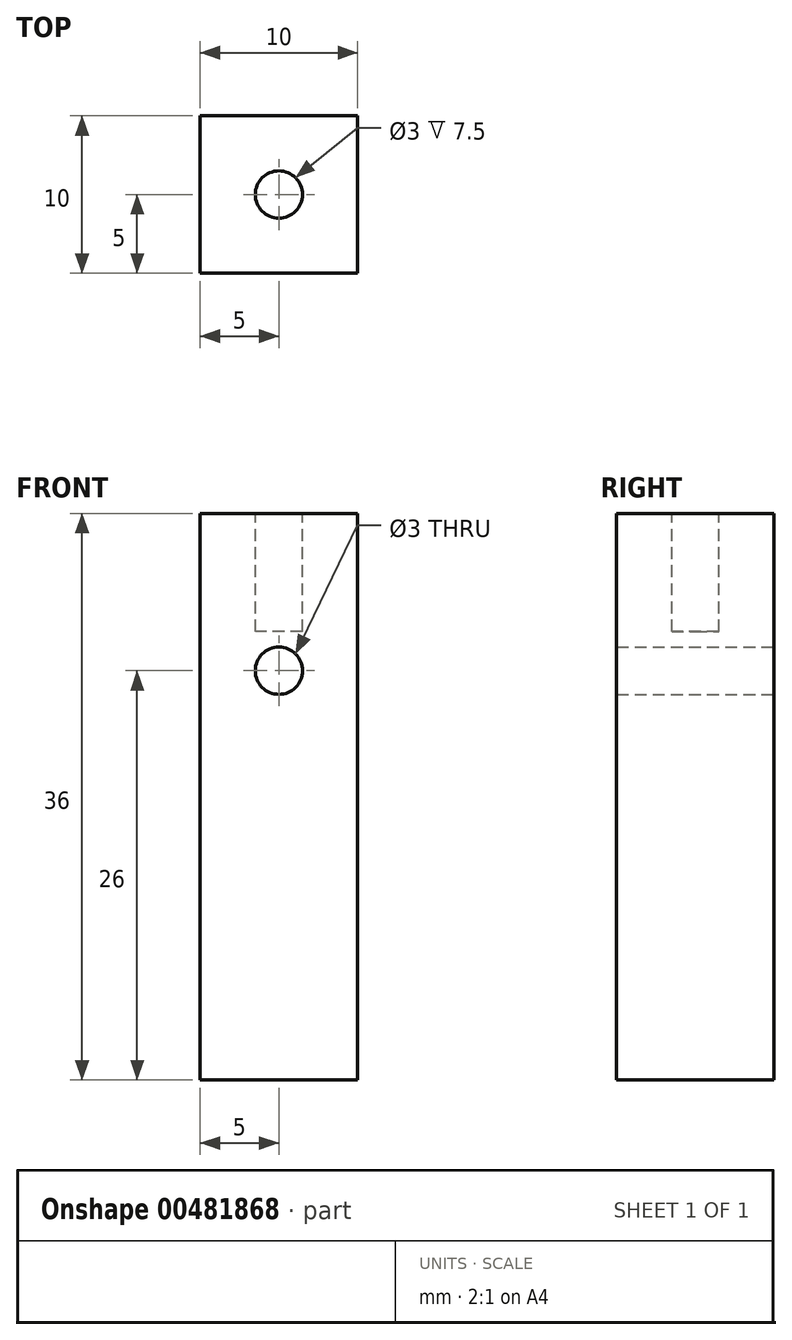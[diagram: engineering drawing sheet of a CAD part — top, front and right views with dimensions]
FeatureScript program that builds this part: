
annotation { "Feature Type Name" : "Feature", "Feature Type Description" : "" }
export const myFeature = defineFeature(function(context is Context, id is Id, definition is map)
    precondition{}
    {
        {
            var Q0;
            Q0=qCreatedBy(makeId("Top.planeOp"),FACE);
            var sketch = newSketch(context, id + "F0", { "sketchPlane" : qUnion([Q0])});
            skLineSegment(sketch, "E0.bottom", {"start": v(-5, -5) * mm, "end": v(5, -5) * mm});
            skLineSegment(sketch, "E0.top", {"start": v(-5, 5) * mm, "end": v(5, 5) * mm});
            skLineSegment(sketch, "E0.left", {"start": v(-5, -5) * mm, "end": v(-5, 5) * mm});
            skLineSegment(sketch, "E0.right", {"start": v(5, -5) * mm, "end": v(5, 5) * mm});
            skPoint(sketch, "E0.middle", {"position": v(0, 0) * mm});
            skSolve(sketch);
        }
        {
            var Q0;
            Q0 = qSketchRegion(id + "F0", true);
            extrude(context, id + "F1", {"entities" : qUnion([Q0]), "endBound" : BoundingType.SYMMETRIC, "depth" : 36 * mm});
        }
        {
            var Q0;
            Q0=makeQuery(id+"F1.opExtrude","CAP_FACE",FACE,{"disambiguationData":[OSD([sQuery(id+"F0.wireOp",EDGE,"E0.bottom"),sQuery(id+"F0.wireOp",EDGE,"E0.top"),sQuery(id+"F0.wireOp",EDGE,"E0.left"),sQuery(id+"F0.wireOp",EDGE,"E0.right")])],"isStart":false});
            var sketch = newSketch(context, id + "F2", { "sketchPlane" : qUnion([Q0])});
            skCircle(sketch, "E1", {"center": v(0, 0) * mm, "radius": 1.5 * mm});
            skSolve(sketch);
        }
        {
            var Q0;
            Q0 = qSketchRegion(id + "F2", true);
            extrude(context, id + "F3", {"entities" : qUnion([Q0]), "operationType" : NewBodyOperationType.REMOVE, "oppositeDirection" : true, "depth" : 7.5 * mm});
        }
        {
            var Q0;
            Q0=qCreatedBy(makeId("Front.planeOp"),FACE);
            var sketch = newSketch(context, id + "F4", { "sketchPlane" : qUnion([Q0])});
            skCircle(sketch, "E2", {"center": v(0, 8) * mm, "radius": 1.5 * mm});
            skSolve(sketch);
        }
        {
            var Q0;
            Q0 = qSketchRegion(id + "F4", true);
            extrude(context, id + "F5", {"entities" : qUnion([Q0]), "operationType" : NewBodyOperationType.REMOVE, "endBound" : BoundingType.SYMMETRIC, "depth" : 25 * mm});
        }
    });
